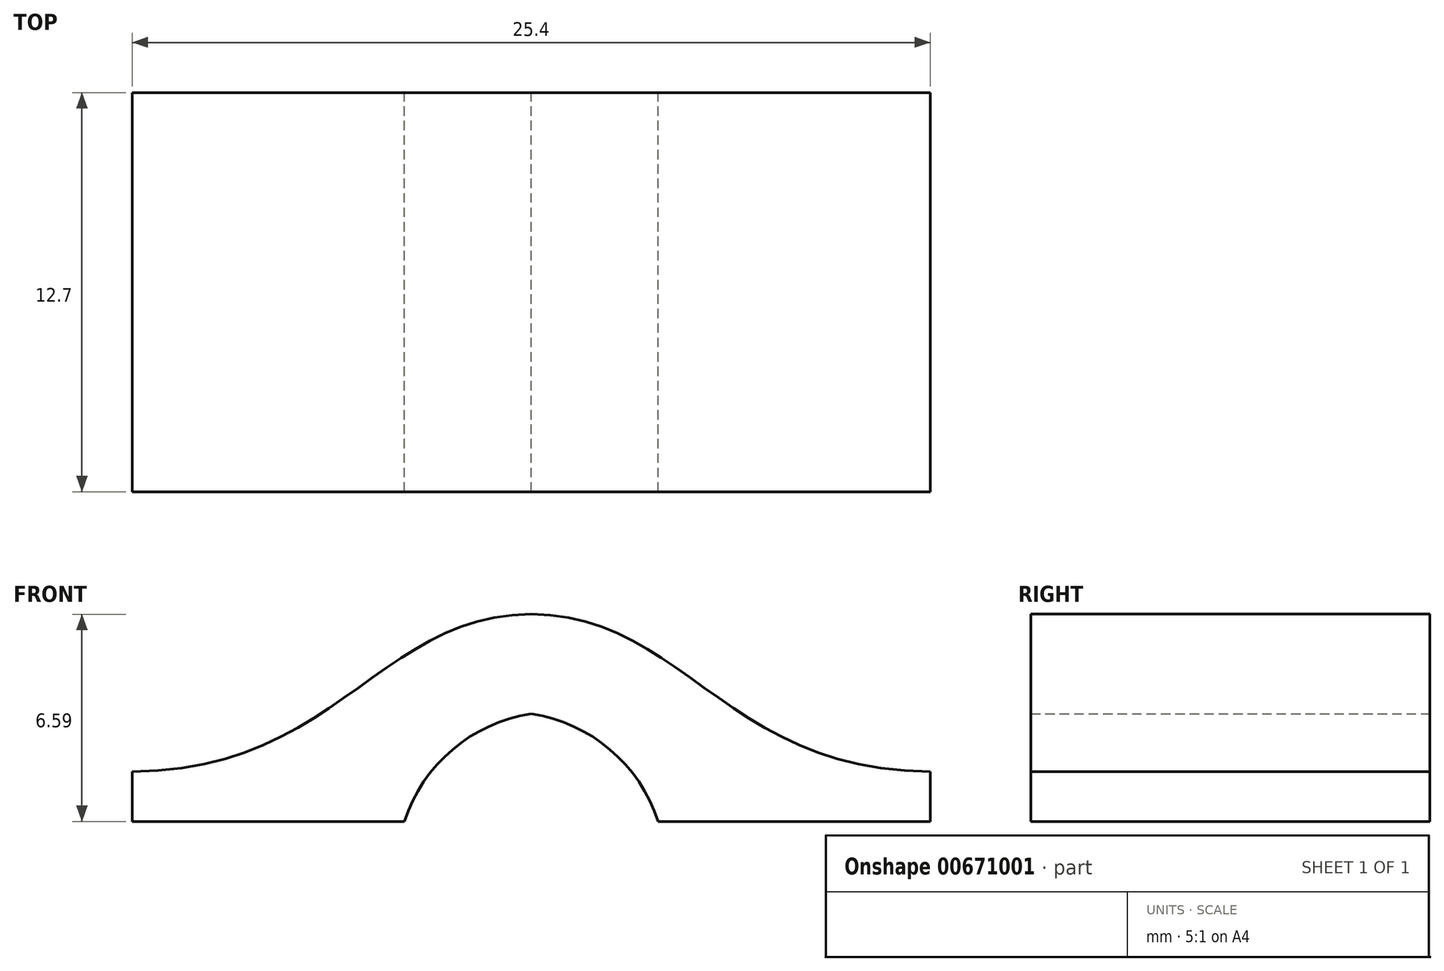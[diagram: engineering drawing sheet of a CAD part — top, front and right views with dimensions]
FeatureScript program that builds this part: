
annotation { "Feature Type Name" : "Feature", "Feature Type Description" : "" }
export const myFeature = defineFeature(function(context is Context, id is Id, definition is map)
    precondition{}
    {
        {
            var Q0;
            Q0=qCreatedBy(makeId("Front.planeOp"),FACE);
            var sketch = newSketch(context, id + "F0", { "sketchPlane" : qUnion([Q0])});
            skLineSegment(sketch, "E0", {"start": v(-12.7, 0) * mm, "end": v(-4.04, 0) * mm});
            skArc(sketch, "E1", {"start": v(0, 3.42) * mm, "mid": v(-2.5, 2.29) * mm, "end": v(-4.04, 0) * mm});
            skLineSegment(sketch, "E2", {"start": v(-12.7, 0) * mm, "end": v(-12.7, 1.59) * mm});
            skLineSegment(sketch, "E3", {"start": v(0, 3.42) * mm, "end": v(0, 6.6) * mm});
            skFitSpline(sketch, "E4", {"points": [v(-12.7, 1.59) * mm, v(0, 6.6) * mm], "startDerivative": vector(19.36, 0) * mm, "endDerivative": vector(14.42, 0) * mm});
            skLineSegment(sketch, "E5", {"start": v(0, 6.6) * mm, "end": v(3.92, 6.6) * mm, "construction": true});
            skLineSegment(sketch, "E6", {"start": v(-12.7, 1.59) * mm, "end": v(-17.11, 1.59) * mm, "construction": true});
            skLineSegment(sketch, "E7.MirrorCS", {"start": v(12.7, 0) * mm, "end": v(12.7, 1.59) * mm});
            skLineSegment(sketch, "E8.MirrorCS", {"start": v(12.7, 0) * mm, "end": v(4.04, 0) * mm});
            skArc(sketch, "E9.MirrorCS", {"start": v(0, 3.42) * mm, "mid": v(2.5, 2.29) * mm, "end": v(4.04, 0) * mm});
            skFitSpline(sketch, "E10.MirrorCS", {"points": [v(12.7, 1.59) * mm, v(0, 6.6) * mm], "startDerivative": vector(-19.36, 0) * mm, "endDerivative": vector(-14.42, 0) * mm});
            skLineSegment(sketch, "E11.MirrorCS", {"start": v(0, 6.6) * mm, "end": v(-3.92, 6.6) * mm, "construction": true});
            skLineSegment(sketch, "E12.MirrorCS", {"start": v(12.7, 1.59) * mm, "end": v(17.11, 1.59) * mm, "construction": true});
            skSolve(sketch);
        }
        {
            var Q0;
            Q0 = qSketchRegion(id + "F0", true);
            extrude(context, id + "F1", {"entities" : qUnion([Q0]), "depth" : 12.7 * mm, "offsetDistance" : 25.4 * mm});
        }
    });
